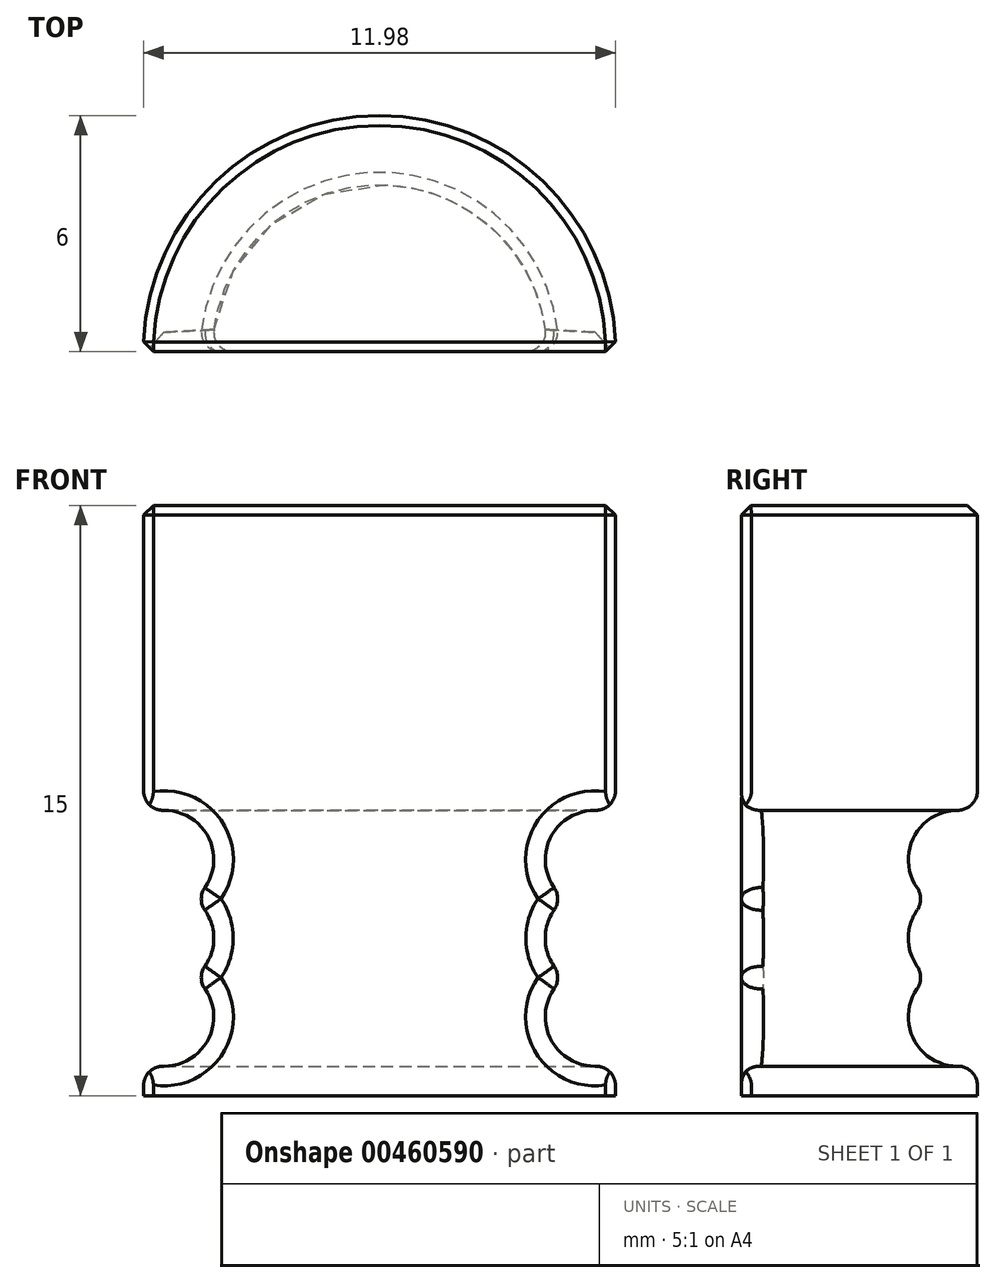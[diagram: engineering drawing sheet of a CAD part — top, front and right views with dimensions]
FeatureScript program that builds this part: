
annotation { "Feature Type Name" : "Feature", "Feature Type Description" : "" }
export const myFeature = defineFeature(function(context is Context, id is Id, definition is map)
    precondition{}
    {
        {
            var Q0;
            Q0=qCreatedBy(makeId("Top.planeOp"),FACE);
            var sketch = newSketch(context, id + "F0", { "sketchPlane" : qUnion([Q0])});
            skArc(sketch, "E0", {"start": v(6, 0) * mm, "mid": v(0, 6) * mm, "end": v(-6, 0) * mm});
            skLineSegment(sketch, "E1", {"start": v(-6, 0) * mm, "end": v(6, 0) * mm});
            skSolve(sketch);
        }
        {
            var Q0;
            Q0=makeQuery(id+"F0.imprint","IMPRINT",FACE,{"disambiguationData":[TD([[makeQuery(id+"F0.imprint","IMPRINT",EDGE,{"derivedFrom":sQuery(id+"F0.wireOp",EDGE,"E0")}),1.0]])]});
            var Q1;
            Q1=sQuery(id+"F0.wireOp",EDGE,"E0");
            var Q2;
            Q2=sQuery(id+"F0.wireOp",EDGE,"E1");
            extrude(context, id + "F1", {"entities" : qUnion([Q0]), "surfaceEntities" : qUnion([Q1, Q2]), "depth" : 15 * mm});
        }
        {
            var Q0;
            Q0=makeQuery(id+"F1.opExtrude","CAP_EDGE",EDGE,{"disambiguationData":[OSD([sQuery(id+"F0.wireOp",EDGE,"E0")])],"isStart":false});
            var Q1;
            Q1=makeQuery(id+"F1.opExtrude","CAP_EDGE",EDGE,{"disambiguationData":[OSD([sQuery(id+"F0.wireOp",EDGE,"E1")])],"isStart":false});
            var Q2;
            {var subQ0=sQuery(id+"F0.wireOp",EDGE,"E1");var subQ1=sQuery(id+"F0.wireOp",EDGE,"E0");Q2=makeQuery(id+"F1.opExtrude","SWEPT_EDGE",EDGE,{"disambiguationData":[OSD([subQ1,subQ0]),TDD([makeQuery(id+"F0.imprint","INTERSECT",VERTEX,{"disambiguationData":[OD(0.0)],"derivedFrom":[subQ1,subQ0]})])]});}
            var Q3;
            {var subQ0=sQuery(id+"F0.wireOp",EDGE,"E1");var subQ1=sQuery(id+"F0.wireOp",EDGE,"E0");Q3=makeQuery(id+"F1.opExtrude","SWEPT_EDGE",EDGE,{"disambiguationData":[OSD([subQ1,subQ0]),TDD([makeQuery(id+"F0.imprint","INTERSECT",VERTEX,{"disambiguationData":[OD(1.0)],"derivedFrom":[subQ1,subQ0]})])]});}
            chamfer(context, id + "F2", {"entities" : qUnion([Q0, Q1, Q2, Q3]), "width" : .25 * mm, "tangentPropagation" : true});
        }
        {
            var Q0;
            Q0=makeQuery(id+"F1.opExtrude","SWEPT_FACE",FACE,{"disambiguationData":[OSD([sQuery(id+"F0.wireOp",EDGE,"E1")])]});
            var sketch = newSketch(context, id + "F3", { "sketchPlane" : qUnion([Q0])});
            skCircle(sketch, "E2", {"center": v(5.5, 2) * mm, "radius": 1.25 * mm});
            skCircle(sketch, "E3", {"center": v(5.5, 4) * mm, "radius": 1.25 * mm});
            skCircle(sketch, "E4", {"center": v(5.5, 6) * mm, "radius": 1.25 * mm});
            skLineSegment(sketch, "E5", {"start": v(0, 0) * mm, "end": v(0, 14.75) * mm, "construction": true});
            skCircle(sketch, "E6.MirrorC", {"center": v(-5.5, 6) * mm, "radius": 1.25 * mm});
            skCircle(sketch, "E7.MirrorC", {"center": v(-5.5, 4) * mm, "radius": 1.25 * mm});
            skCircle(sketch, "E8.MirrorC", {"center": v(-5.5, 2) * mm, "radius": 1.25 * mm});
            skSolve(sketch);
        }
        {
            var Q0;
            {var subQ0=sQuery(id+"F3.wireOp",EDGE,"E4");var subQ1=sQuery(id+"F3.wireOp",EDGE,"E3");var subQ2=makeQuery(id+"F3.imprint","INTERSECT",VERTEX,{"disambiguationData":[OD(1.0)],"derivedFrom":[subQ1,subQ0]});Q0=makeQuery(id+"F3.imprint","IMPRINT",FACE,{"disambiguationData":[TD([[makeQuery(id+"F3.imprint","IMPRINT",EDGE,{"disambiguationData":[TD([[subQ2,1.0]])],"derivedFrom":subQ1}),-1.0]])]});}
            var Q1;
            {var subQ0=sQuery(id+"F3.wireOp",EDGE,"E4");var subQ1=sQuery(id+"F3.wireOp",EDGE,"E3");var subQ2=makeQuery(id+"F3.imprint","INTERSECT",VERTEX,{"disambiguationData":[OD(1.0)],"derivedFrom":[subQ1,subQ0]});Q1=makeQuery(id+"F3.imprint","IMPRINT",FACE,{"disambiguationData":[TD([[makeQuery(id+"F3.imprint","IMPRINT",EDGE,{"disambiguationData":[TD([[subQ2,1.0]])],"derivedFrom":subQ1}),1.0]])]});}
            var Q2;
            {var subQ0=sQuery(id+"F3.wireOp",EDGE,"E4");var subQ1=sQuery(id+"F3.wireOp",EDGE,"E3");var subQ2=makeQuery(id+"F3.imprint","INTERSECT",VERTEX,{"disambiguationData":[OD(0.0)],"derivedFrom":[subQ1,subQ0]});Q2=makeQuery(id+"F3.imprint","IMPRINT",FACE,{"disambiguationData":[TD([[makeQuery(id+"F3.imprint","IMPRINT",EDGE,{"disambiguationData":[TD([[subQ2,-1.0]])],"derivedFrom":subQ1}),-1.0]])]});}
            var Q3;
            {var subQ0=sQuery(id+"F3.wireOp",EDGE,"E4");var subQ1=sQuery(id+"F3.wireOp",EDGE,"E3");var subQ2=makeQuery(id+"F3.imprint","INTERSECT",VERTEX,{"disambiguationData":[OD(0.0)],"derivedFrom":[subQ1,subQ0]});Q3=makeQuery(id+"F3.imprint","IMPRINT",FACE,{"disambiguationData":[TD([[makeQuery(id+"F3.imprint","IMPRINT",EDGE,{"disambiguationData":[TD([[subQ2,-1.0]])],"derivedFrom":subQ1}),1.0]])]});}
            var Q4;
            {var subQ0=sQuery(id+"F3.wireOp",EDGE,"E3");var subQ1=sQuery(id+"F3.wireOp",EDGE,"E2");var subQ2=makeQuery(id+"F3.imprint","INTERSECT",VERTEX,{"disambiguationData":[OD(0.0)],"derivedFrom":[subQ1,subQ0]});Q4=makeQuery(id+"F3.imprint","IMPRINT",FACE,{"disambiguationData":[TD([[makeQuery(id+"F3.imprint","IMPRINT",EDGE,{"disambiguationData":[TD([[subQ2,-1.0]])],"derivedFrom":subQ0}),1.0]])]});}
            var Q5;
            {var subQ0=sQuery(id+"F3.wireOp",EDGE,"E3");var subQ1=sQuery(id+"F3.wireOp",EDGE,"E2");var subQ2=makeQuery(id+"F3.imprint","INTERSECT",VERTEX,{"disambiguationData":[OD(1.0)],"derivedFrom":[subQ1,subQ0]});Q5=makeQuery(id+"F3.imprint","IMPRINT",FACE,{"disambiguationData":[TD([[makeQuery(id+"F3.imprint","IMPRINT",EDGE,{"disambiguationData":[TD([[subQ2,1.0]])],"derivedFrom":subQ0}),1.0]])]});}
            var Q6;
            {var subQ0=sQuery(id+"F3.wireOp",EDGE,"E3");var subQ1=sQuery(id+"F3.wireOp",EDGE,"E2");var subQ2=makeQuery(id+"F3.imprint","INTERSECT",VERTEX,{"disambiguationData":[OD(0.0)],"derivedFrom":[subQ1,subQ0]});Q6=makeQuery(id+"F3.imprint","IMPRINT",FACE,{"disambiguationData":[TD([[makeQuery(id+"F3.imprint","IMPRINT",EDGE,{"disambiguationData":[TD([[subQ2,-1.0]])],"derivedFrom":subQ1}),1.0]])]});}
            var Q7;
            {var subQ0=sQuery(id+"F3.wireOp",EDGE,"E3");var subQ1=sQuery(id+"F3.wireOp",EDGE,"E2");var subQ2=makeQuery(id+"F3.imprint","INTERSECT",VERTEX,{"disambiguationData":[OD(1.0)],"derivedFrom":[subQ1,subQ0]});Q7=makeQuery(id+"F3.imprint","IMPRINT",FACE,{"disambiguationData":[TD([[makeQuery(id+"F3.imprint","IMPRINT",EDGE,{"disambiguationData":[TD([[subQ2,1.0]])],"derivedFrom":subQ1}),1.0]])]});}
            var Q8;
            {var subQ0=sQuery(id+"F3.wireOp",EDGE,"E3");var subQ1=sQuery(id+"F3.wireOp",EDGE,"E2");var subQ2=makeQuery(id+"F3.imprint","INTERSECT",VERTEX,{"disambiguationData":[OD(0.0)],"derivedFrom":[subQ1,subQ0]});Q8=makeQuery(id+"F3.imprint","IMPRINT",FACE,{"disambiguationData":[TD([[makeQuery(id+"F3.imprint","IMPRINT",EDGE,{"disambiguationData":[TD([[subQ2,1.0]])],"derivedFrom":subQ1}),1.0]])]});}
            var Q9;
            {var subQ0=sQuery(id+"F3.wireOp",EDGE,"E3");var subQ1=sQuery(id+"F3.wireOp",EDGE,"E2");var subQ2=makeQuery(id+"F3.imprint","INTERSECT",VERTEX,{"disambiguationData":[OD(1.0)],"derivedFrom":[subQ1,subQ0]});Q9=makeQuery(id+"F3.imprint","IMPRINT",FACE,{"disambiguationData":[TD([[makeQuery(id+"F3.imprint","IMPRINT",EDGE,{"disambiguationData":[TD([[subQ2,-1.0]])],"derivedFrom":subQ1}),1.0]])]});}
            var Q10;
            Q10=sQuery(id+"F3.wireOp",EDGE,"E5");
            revolve(context, id + "F4", {"operationType" : NewBodyOperationType.REMOVE, "entities" : qUnion([Q0, Q1, Q2, Q3, Q4, Q5, Q6, Q7, Q8, Q9]), "axis" : qUnion([Q10]), "revolveType" : RevolveType.FULL, "oppositeDirection" : true});
        }
        {
            var Q0;
            Q0=makeQuery(id+"F4.boolean.opBoolean","INTERSECT",EDGE,{"derivedFrom":[makeQuery(id+"F1.opExtrude","SWEPT_FACE",FACE,{"disambiguationData":[OSD([sQuery(id+"F0.wireOp",EDGE,"E0")])]}),makeQuery(id+"F4.opRevolve","SWEPT_FACE",FACE,{"disambiguationData":[OSD([sQuery(id+"F3.wireOp",EDGE,"E4")])]})]});
            var Q1;
            {var subQ0=sQuery(id+"F3.wireOp",EDGE,"E4");var subQ1=sQuery(id+"F3.wireOp",EDGE,"E3");Q1=makeQuery(id+"F4.boolean.opBoolean","COPY",EDGE,{"derivedFrom":makeQuery(id+"F4.opRevolve","SWEPT_EDGE",EDGE,{"disambiguationData":[OSD([subQ1,subQ0]),TDD([makeQuery(id+"F3.imprint","INTERSECT",VERTEX,{"disambiguationData":[OD(1.0)],"derivedFrom":[subQ1,subQ0]})])]})});}
            var Q2;
            {var subQ0=sQuery(id+"F3.wireOp",EDGE,"E3");var subQ1=sQuery(id+"F3.wireOp",EDGE,"E2");Q2=makeQuery(id+"F4.boolean.opBoolean","COPY",EDGE,{"derivedFrom":makeQuery(id+"F4.opRevolve","SWEPT_EDGE",EDGE,{"disambiguationData":[OSD([subQ1,subQ0]),TDD([makeQuery(id+"F3.imprint","INTERSECT",VERTEX,{"disambiguationData":[OD(1.0)],"derivedFrom":[subQ1,subQ0]})])]})});}
            var Q3;
            Q3=makeQuery(id+"F4.boolean.opBoolean","INTERSECT",EDGE,{"derivedFrom":[makeQuery(id+"F1.opExtrude","SWEPT_FACE",FACE,{"disambiguationData":[OSD([sQuery(id+"F0.wireOp",EDGE,"E0")])]}),makeQuery(id+"F4.opRevolve","SWEPT_FACE",FACE,{"disambiguationData":[OSD([sQuery(id+"F3.wireOp",EDGE,"E2")])]})]});
            var Q4;
            Q4=makeQuery(id+"F4.boolean.opBoolean","INTERSECT",EDGE,{"disambiguationData":[OD(0.0)],"derivedFrom":[makeQuery(id+"F1.opExtrude","SWEPT_FACE",FACE,{"disambiguationData":[OSD([sQuery(id+"F0.wireOp",EDGE,"E1")])]}),makeQuery(id+"F4.opRevolve","SWEPT_FACE",FACE,{"disambiguationData":[OSD([sQuery(id+"F3.wireOp",EDGE,"E4")])]})]});
            var Q5;
            {var subQ0=sQuery(id+"F3.wireOp",EDGE,"E3");Q5=makeQuery(id+"F4.boolean.opBoolean","INTERSECT",EDGE,{"disambiguationData":[OD(0.0)],"derivedFrom":[makeQuery(id+"F1.opExtrude","SWEPT_FACE",FACE,{"disambiguationData":[OSD([sQuery(id+"F0.wireOp",EDGE,"E1")])]}),makeQuery(id+"F4.opRevolve","SWEPT_FACE",FACE,{"disambiguationData":[OSD([subQ0]),TDD([makeQuery(id+"F3.imprint","IMPRINT",EDGE,{"disambiguationData":[TD([[makeQuery(id+"F3.imprint","INTERSECT",VERTEX,{"disambiguationData":[OD(1.0)],"derivedFrom":[sQuery(id+"F3.wireOp",EDGE,"E2"),subQ0]}),1.0]])],"derivedFrom":subQ0})])]})]});}
            var Q6;
            Q6=makeQuery(id+"F4.boolean.opBoolean","INTERSECT",EDGE,{"disambiguationData":[OD(0.0)],"derivedFrom":[makeQuery(id+"F1.opExtrude","SWEPT_FACE",FACE,{"disambiguationData":[OSD([sQuery(id+"F0.wireOp",EDGE,"E1")])]}),makeQuery(id+"F4.opRevolve","SWEPT_FACE",FACE,{"disambiguationData":[OSD([sQuery(id+"F3.wireOp",EDGE,"E2")])]})]});
            var Q7;
            Q7=makeQuery(id+"F4.boolean.opBoolean","INTERSECT",EDGE,{"disambiguationData":[OD(1.0)],"derivedFrom":[makeQuery(id+"F1.opExtrude","SWEPT_FACE",FACE,{"disambiguationData":[OSD([sQuery(id+"F0.wireOp",EDGE,"E1")])]}),makeQuery(id+"F4.opRevolve","SWEPT_FACE",FACE,{"disambiguationData":[OSD([sQuery(id+"F3.wireOp",EDGE,"E2")])]})]});
            var Q8;
            {var subQ0=sQuery(id+"F3.wireOp",EDGE,"E3");Q8=makeQuery(id+"F4.boolean.opBoolean","INTERSECT",EDGE,{"disambiguationData":[OD(1.0)],"derivedFrom":[makeQuery(id+"F1.opExtrude","SWEPT_FACE",FACE,{"disambiguationData":[OSD([sQuery(id+"F0.wireOp",EDGE,"E1")])]}),makeQuery(id+"F4.opRevolve","SWEPT_FACE",FACE,{"disambiguationData":[OSD([subQ0]),TDD([makeQuery(id+"F3.imprint","IMPRINT",EDGE,{"disambiguationData":[TD([[makeQuery(id+"F3.imprint","INTERSECT",VERTEX,{"disambiguationData":[OD(1.0)],"derivedFrom":[sQuery(id+"F3.wireOp",EDGE,"E2"),subQ0]}),1.0]])],"derivedFrom":subQ0})])]})]});}
            var Q9;
            Q9=makeQuery(id+"F4.boolean.opBoolean","INTERSECT",EDGE,{"disambiguationData":[OD(1.0)],"derivedFrom":[makeQuery(id+"F1.opExtrude","SWEPT_FACE",FACE,{"disambiguationData":[OSD([sQuery(id+"F0.wireOp",EDGE,"E1")])]}),makeQuery(id+"F4.opRevolve","SWEPT_FACE",FACE,{"disambiguationData":[OSD([sQuery(id+"F3.wireOp",EDGE,"E4")])]})]});
            fillet(context, id + "F5", {"entities" : qUnion([Q0, Q1, Q2, Q3, Q4, Q5, Q6, Q7, Q8, Q9]), "radius" : .5 * mm, "tangentPropagation" : true, "allowEdgeOverflow" : false});
        }
    });
